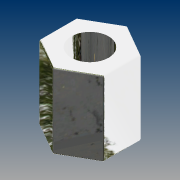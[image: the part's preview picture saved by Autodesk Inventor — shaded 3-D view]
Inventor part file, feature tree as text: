
AUTODESK INVENTOR PART (.ipt)
format: ipt  version: 2014 (Build 180170000, 170)  size: 138,240 bytes
history: native  units: mm
features: extrude x2, fillet x2, sketch x2
ambient origin geometry x8: Origin, YZ Plane, XZ Plane, XY Plane, X Axis, Y Axis, Z Axis, Center Point
bodies: Solid1 (feature_tree)
feature tree (6):
  extrude  "Extrusion1"  Depth=100.0mm
  extrude  "Extrusion2"  TaperAngle=0.0deg  [1 undecoded]
  fillet  "Fillet1"  Radius=100.0mm
  fillet  "Fillet2"  Radius=2.0mm
  sketch  "Sketch1"  dims[d0=100.0mm d1=50.0mm]
  sketch  "Sketch2"  dims[d2=100.0mm d3=0.0mm d4=0.0mm d5=100.0mm d6=0.0mm d7=2.0mm d8=2.0mm]
note: 1 required parameter value undecoded (feature->parameter linkage not recoverable at this tier; creation-order binding heuristic only, values carry confidence <= 0.55)
